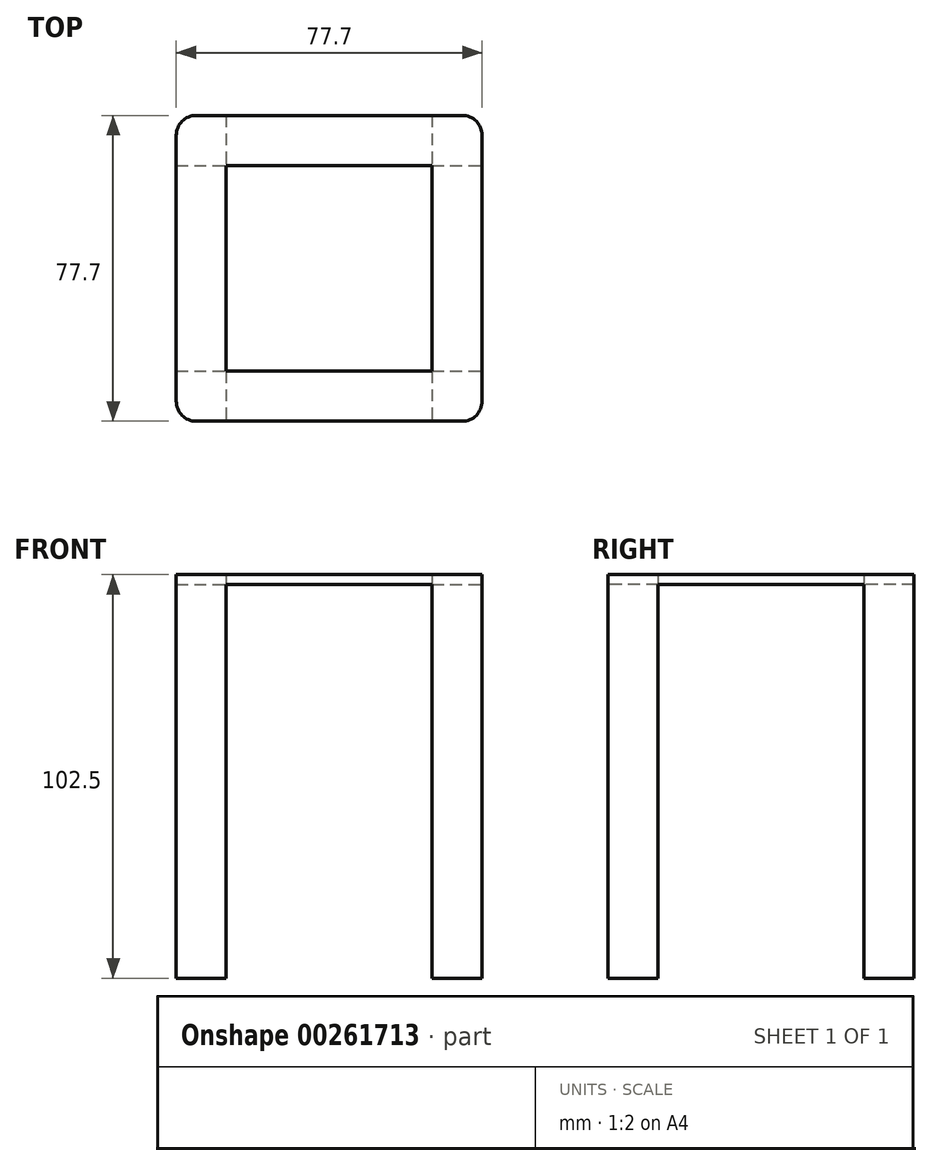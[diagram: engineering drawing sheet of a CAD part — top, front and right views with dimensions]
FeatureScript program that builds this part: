
annotation { "Feature Type Name" : "Feature", "Feature Type Description" : "" }
export const myFeature = defineFeature(function(context is Context, id is Id, definition is map)
    precondition{}
    {
        {
            var Q0;
            Q0=qCreatedBy(makeId("Top.planeOp"),FACE);
            var sketch = newSketch(context, id + "F0", { "sketchPlane" : qUnion([Q0])});
            skLineSegment(sketch, "E0.bottom", {"start": v(-38.85, 38.85) * mm, "end": v(-26.15, 38.85) * mm});
            skLineSegment(sketch, "E0.top", {"start": v(-38.85, 26.15) * mm, "end": v(-26.15, 26.15) * mm});
            skLineSegment(sketch, "E0.left", {"start": v(-38.85, 38.85) * mm, "end": v(-38.85, 26.15) * mm});
            skLineSegment(sketch, "E0.right", {"start": v(-26.15, 38.85) * mm, "end": v(-26.15, 26.15) * mm});
            skPoint(sketch, "E0.middle", {"position": v(-32.5, 32.5) * mm});
            skLineSegment(sketch, "E1.bottom", {"start": v(26.15, 38.85) * mm, "end": v(38.85, 38.85) * mm});
            skLineSegment(sketch, "E1.top", {"start": v(26.15, 26.15) * mm, "end": v(38.85, 26.15) * mm});
            skLineSegment(sketch, "E1.left", {"start": v(26.15, 38.85) * mm, "end": v(26.15, 26.15) * mm});
            skLineSegment(sketch, "E1.right", {"start": v(38.85, 38.85) * mm, "end": v(38.85, 26.15) * mm});
            skPoint(sketch, "E1.middle", {"position": v(32.5, 32.5) * mm});
            skLineSegment(sketch, "E2.bottom", {"start": v(26.15, -26.15) * mm, "end": v(38.85, -26.15) * mm});
            skLineSegment(sketch, "E2.top", {"start": v(26.15, -38.85) * mm, "end": v(38.85, -38.85) * mm});
            skLineSegment(sketch, "E2.left", {"start": v(26.15, -26.15) * mm, "end": v(26.15, -38.85) * mm});
            skLineSegment(sketch, "E2.right", {"start": v(38.85, -26.15) * mm, "end": v(38.85, -38.85) * mm});
            skPoint(sketch, "E2.middle", {"position": v(32.5, -32.5) * mm});
            skLineSegment(sketch, "E3.bottom", {"start": v(-38.85, -26.15) * mm, "end": v(-26.15, -26.15) * mm});
            skLineSegment(sketch, "E3.top", {"start": v(-38.85, -38.85) * mm, "end": v(-26.15, -38.85) * mm});
            skLineSegment(sketch, "E3.left", {"start": v(-38.85, -26.15) * mm, "end": v(-38.85, -38.85) * mm});
            skLineSegment(sketch, "E3.right", {"start": v(-26.15, -26.15) * mm, "end": v(-26.15, -38.85) * mm});
            skPoint(sketch, "E3.middle", {"position": v(-32.5, -32.5) * mm});
            skSolve(sketch);
        }
        {
            var Q0;
            Q0=makeQuery(id+"F0.imprint","IMPRINT",FACE,{"disambiguationData":[TD([[makeQuery(id+"F0.imprint","IMPRINT",EDGE,{"derivedFrom":sQuery(id+"F0.wireOp",EDGE,"E0.bottom")}),-1.0]])]});
            var Q1;
            Q1=makeQuery(id+"F0.imprint","IMPRINT",FACE,{"disambiguationData":[TD([[makeQuery(id+"F0.imprint","IMPRINT",EDGE,{"derivedFrom":sQuery(id+"F0.wireOp",EDGE,"E1.bottom")}),-1.0]])]});
            var Q2;
            Q2=makeQuery(id+"F0.imprint","IMPRINT",FACE,{"disambiguationData":[TD([[makeQuery(id+"F0.imprint","IMPRINT",EDGE,{"derivedFrom":sQuery(id+"F0.wireOp",EDGE,"E2.bottom")}),-1.0]])]});
            var Q3;
            Q3=makeQuery(id+"F0.imprint","IMPRINT",FACE,{"disambiguationData":[TD([[makeQuery(id+"F0.imprint","IMPRINT",EDGE,{"derivedFrom":sQuery(id+"F0.wireOp",EDGE,"E3.bottom")}),-1.0]])]});
            extrude(context, id + "F1", {"entities" : qUnion([Q0, Q1, Q2, Q3]), "depth" : 100 * mm});
        }
        {
            var Q0;
            Q0=makeQuery(id+"F1.opExtrude","CAP_FACE",FACE,{"disambiguationData":[OSD([sQuery(id+"F0.wireOp",EDGE,"E2.bottom"),sQuery(id+"F0.wireOp",EDGE,"E2.top"),sQuery(id+"F0.wireOp",EDGE,"E2.left"),sQuery(id+"F0.wireOp",EDGE,"E2.right")])],"isStart":false});
            var sketch = newSketch(context, id + "F2", { "sketchPlane" : qUnion([Q0])});
            skLineSegment(sketch, "E4.0.0", {"start": v(-38.85, 38.85) * mm, "end": v(-38.85, 26.15) * mm});
            skLineSegment(sketch, "E4.0.1", {"start": v(-38.85, 26.15) * mm, "end": v(-26.15, 26.15) * mm});
            skLineSegment(sketch, "E4.0.2", {"start": v(-26.15, 26.15) * mm, "end": v(-26.15, 38.85) * mm});
            skLineSegment(sketch, "E4.0.3", {"start": v(-26.15, 38.85) * mm, "end": v(-38.85, 38.85) * mm});
            skLineSegment(sketch, "E5.0.0", {"start": v(26.15, 38.85) * mm, "end": v(26.15, 26.15) * mm});
            skLineSegment(sketch, "E5.0.1", {"start": v(26.15, 26.15) * mm, "end": v(38.85, 26.15) * mm});
            skLineSegment(sketch, "E5.0.2", {"start": v(38.85, 26.15) * mm, "end": v(38.85, 38.85) * mm});
            skLineSegment(sketch, "E5.0.3", {"start": v(38.85, 38.85) * mm, "end": v(26.15, 38.85) * mm});
            skLineSegment(sketch, "E6.0.0", {"start": v(-38.85, -26.15) * mm, "end": v(-38.85, -38.85) * mm});
            skLineSegment(sketch, "E6.0.1", {"start": v(-38.85, -38.85) * mm, "end": v(-26.15, -38.85) * mm});
            skLineSegment(sketch, "E6.0.2", {"start": v(-26.15, -38.85) * mm, "end": v(-26.15, -26.15) * mm});
            skLineSegment(sketch, "E6.0.3", {"start": v(-26.15, -26.15) * mm, "end": v(-38.85, -26.15) * mm});
            skLineSegment(sketch, "E7.bottom", {"start": v(38.85, -38.85) * mm, "end": v(-38.85, -38.85) * mm});
            skLineSegment(sketch, "E7.top", {"start": v(38.85, 38.85) * mm, "end": v(-38.85, 38.85) * mm});
            skLineSegment(sketch, "E7.left", {"start": v(38.85, -38.85) * mm, "end": v(38.85, 38.85) * mm});
            skLineSegment(sketch, "E7.right", {"start": v(-38.85, -38.85) * mm, "end": v(-38.85, 38.85) * mm});
            skLineSegment(sketch, "E8", {"start": v(-26.15, 26.15) * mm, "end": v(-26.15, -26.15) * mm});
            skLineSegment(sketch, "E9", {"start": v(-26.15, -26.15) * mm, "end": v(26.15, -26.15) * mm});
            skLineSegment(sketch, "E10", {"start": v(26.15, 26.15) * mm, "end": v(26.15, -26.15) * mm});
            skLineSegment(sketch, "E11", {"start": v(26.15, 26.15) * mm, "end": v(-26.15, 26.15) * mm});
            skSolve(sketch);
        }
        {
            var Q0;
            {var subQ0=sQuery(id+"F2.wireOp",EDGE,"E4.0.1");Q0=makeQuery(id+"F2.imprint","IMPRINT",FACE,{"disambiguationData":[TD([[makeQuery(id+"F2.imprint","IMPRINT",EDGE,{"derivedFrom":subQ0}),-1.0]])]});}
            var Q1;
            {var subQ0=sQuery(id+"F2.wireOp",EDGE,"E4.0.1");Q1=makeQuery(id+"F2.imprint","IMPRINT",FACE,{"disambiguationData":[TD([[makeQuery(id+"F2.imprint","IMPRINT",EDGE,{"derivedFrom":subQ0}),1.0]])]});}
            var Q2;
            {var subQ0=sQuery(id+"F2.wireOp",EDGE,"E4.0.2");Q2=makeQuery(id+"F2.imprint","IMPRINT",FACE,{"disambiguationData":[TD([[makeQuery(id+"F2.imprint","IMPRINT",EDGE,{"derivedFrom":subQ0}),-1.0]])]});}
            var Q3;
            {var subQ0=sQuery(id+"F2.wireOp",EDGE,"E5.0.0");Q3=makeQuery(id+"F2.imprint","IMPRINT",FACE,{"disambiguationData":[TD([[makeQuery(id+"F2.imprint","IMPRINT",EDGE,{"derivedFrom":subQ0}),1.0]])]});}
            var Q4;
            {var subQ0=sQuery(id+"F2.wireOp",EDGE,"E5.0.1");Q4=makeQuery(id+"F2.imprint","IMPRINT",FACE,{"disambiguationData":[TD([[makeQuery(id+"F2.imprint","IMPRINT",EDGE,{"derivedFrom":subQ0}),-1.0]])]});}
            var Q5;
            {var subQ4=makeQuery(id+"F1.opExtrude","CAP_EDGE",EDGE,{"disambiguationData":[OSD([sQuery(id+"F0.wireOp",EDGE,"E2.bottom")])],"isStart":false});Q5=makeQuery(id+"F2.imprint","IMPRINT",FACE,{"disambiguationData":[TD([[makeQuery(id+"F2.imprint","IMPRINT",EDGE,{"derivedFrom":subQ4}),-1.0]])]});}
            var Q6;
            {var subQ0=sQuery(id+"F2.wireOp",EDGE,"E6.0.2");Q6=makeQuery(id+"F2.imprint","IMPRINT",FACE,{"disambiguationData":[TD([[makeQuery(id+"F2.imprint","IMPRINT",EDGE,{"derivedFrom":subQ0}),-1.0]])]});}
            var Q7;
            {var subQ0=sQuery(id+"F2.wireOp",EDGE,"E6.0.2");Q7=makeQuery(id+"F2.imprint","IMPRINT",FACE,{"disambiguationData":[TD([[makeQuery(id+"F2.imprint","IMPRINT",EDGE,{"derivedFrom":subQ0}),1.0]])]});}
            extrude(context, id + "F3", {"entities" : qUnion([Q0, Q1, Q2, Q3, Q4, Q5, Q6, Q7]), "operationType" : NewBodyOperationType.ADD, "depth" : 2.5 * mm});
        }
        {
            var Q0;
            Q0=makeQuery(id+"F3.boolean.opBoolean","MERGE",EDGE,{"derivedFrom":[makeQuery(id+"F1.opExtrude","SWEPT_EDGE",EDGE,{"disambiguationData":[OSD([sQuery(id+"F0.wireOp",EDGE,"E2.top"),sQuery(id+"F0.wireOp",EDGE,"E2.right")])]}),makeQuery(id+"F3.opExtrude","SWEPT_EDGE",EDGE,{"disambiguationData":[OSD([sQuery(id+"F2.wireOp",EDGE,"E7.bottom"),sQuery(id+"F2.wireOp",EDGE,"E7.left")])]})]});
            var Q1;
            Q1=makeQuery(id+"F3.boolean.opBoolean","MERGE",EDGE,{"derivedFrom":[makeQuery(id+"F1.opExtrude","SWEPT_EDGE",EDGE,{"disambiguationData":[OSD([sQuery(id+"F0.wireOp",EDGE,"E1.bottom"),sQuery(id+"F0.wireOp",EDGE,"E1.right")])]}),makeQuery(id+"F3.opExtrude","SWEPT_EDGE",EDGE,{"disambiguationData":[OSD([sQuery(id+"F2.wireOp",EDGE,"E7.top"),sQuery(id+"F2.wireOp",EDGE,"E7.left")])]})]});
            var Q2;
            Q2=makeQuery(id+"F3.boolean.opBoolean","MERGE",EDGE,{"derivedFrom":[makeQuery(id+"F1.opExtrude","SWEPT_EDGE",EDGE,{"disambiguationData":[OSD([sQuery(id+"F0.wireOp",EDGE,"E0.bottom"),sQuery(id+"F0.wireOp",EDGE,"E0.left")])]}),makeQuery(id+"F3.opExtrude","SWEPT_EDGE",EDGE,{"disambiguationData":[OSD([sQuery(id+"F2.wireOp",EDGE,"E7.top"),sQuery(id+"F2.wireOp",EDGE,"E7.right")])]})]});
            var Q3;
            Q3=makeQuery(id+"F3.boolean.opBoolean","MERGE",EDGE,{"derivedFrom":[makeQuery(id+"F1.opExtrude","SWEPT_EDGE",EDGE,{"disambiguationData":[OSD([sQuery(id+"F0.wireOp",EDGE,"E3.top"),sQuery(id+"F0.wireOp",EDGE,"E3.left")])]}),makeQuery(id+"F3.opExtrude","SWEPT_EDGE",EDGE,{"disambiguationData":[OSD([sQuery(id+"F2.wireOp",EDGE,"E7.bottom"),sQuery(id+"F2.wireOp",EDGE,"E7.right")])]})]});
            fillet(context, id + "F4", {"entities" : qUnion([Q0, Q1, Q2, Q3]), "radius" : 5.08 * mm, "tangentPropagation" : true, "allowEdgeOverflow" : false});
        }
    });
